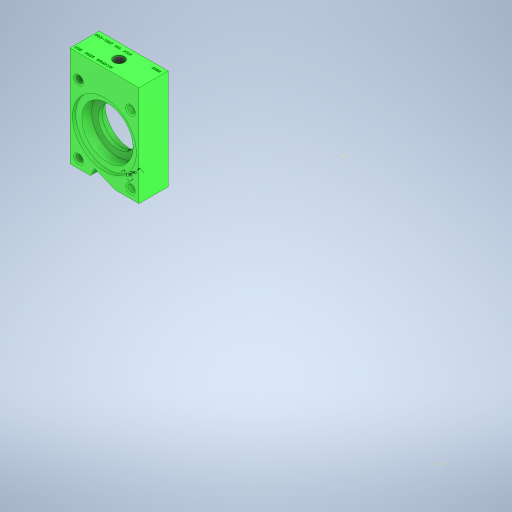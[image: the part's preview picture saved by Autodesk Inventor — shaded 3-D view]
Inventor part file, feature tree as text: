
AUTODESK INVENTOR PART (.ipt)
format: ipt  version: 2024.1 (Build 281209000, 209)  size: 710,144 bytes
history: native  units: in
note: dims shown in document units (in); Inventor stores cm internally (conversion verified against a paired STEP export)
features: hole x7, extrude x4, sketch x4, fillet x1
ambient origin geometry x8: Origin, YZ Plane, XZ Plane, XY Plane, X Axis, Y Axis, Z Axis, Center Point
bodies: Solid1 (feature_tree)
feature tree (16):
  extrude  "Extrusion1"  Depth=0.5in TaperAngle=0.0deg
  extrude  "Extrusion2"  Depth=0.25in
  extrude  "Extrusion3"  Depth=0.25in
  hole  "Hole1"  [1 undecoded]
  hole  "Hole2"  [1 undecoded]
  extrude  "Extrusion4"  Depth=0.25in
  hole  "Hole5"  [1 undecoded]
  hole  "Hole6"  [1 undecoded]
  fillet  "Fillet1"  Radius=1.0in
  hole  "Hole7"  [1 undecoded]
  hole  "Hole3"  [1 undecoded]
  hole  "Hole4"  [1 undecoded]
  sketch  "Sketch1"  dims[d0=0.5in d1=0.0in d2=0.4in d3=0.0in]
  sketch  "Sketch2"  dims[d4=0.6in d5=0.0in]
  sketch  "Sketch5"  dims[d6=0.211in d7=0.25in d8=0.507in d9=0.25in d10=0.5635in d11=0.25in d12=0.0in]
  sketch  "Sketch7"  dims[d13=0.06in d14=0.75in d15=0.507in d16=0.25in d17=0.5635in d18=1.0in d19=0.8108in d20=0.4583in d21=0.29in d22=0.04in d23=0.75in d24=0.507in d25=0.25in d26=0.5635in d27=1.0in d28=0.8108in d29=0.213in d30=0.75in d31=0.507in d32=0.25in d33=0.5635in d34=0.25in d35=0.0in d36=0.75in d38=135.0deg d39=0.4583in d40=112.5deg d41=0.25in d42=1.0in d43=0.0in d44=0.29in d45=0.196in d46=0.211in d47=0.25in d48=0.375in d49=0.25in d50=0.5635in d51=0.25in d52=0.0in d53=0.06in d54=0.75in d55=0.375in d56=0.25in d57=0.5635in d58=0.6in d59=0.8108in d60=0.0312in d61=0.13in d62=1.0in d63=0.375in d64=0.25in d65=0.5635in d66=1.0in d67=0.8108in]
note: 7 required parameter values undecoded (feature->parameter linkage not recoverable at this tier; creation-order binding heuristic only, values carry confidence <= 0.55)
